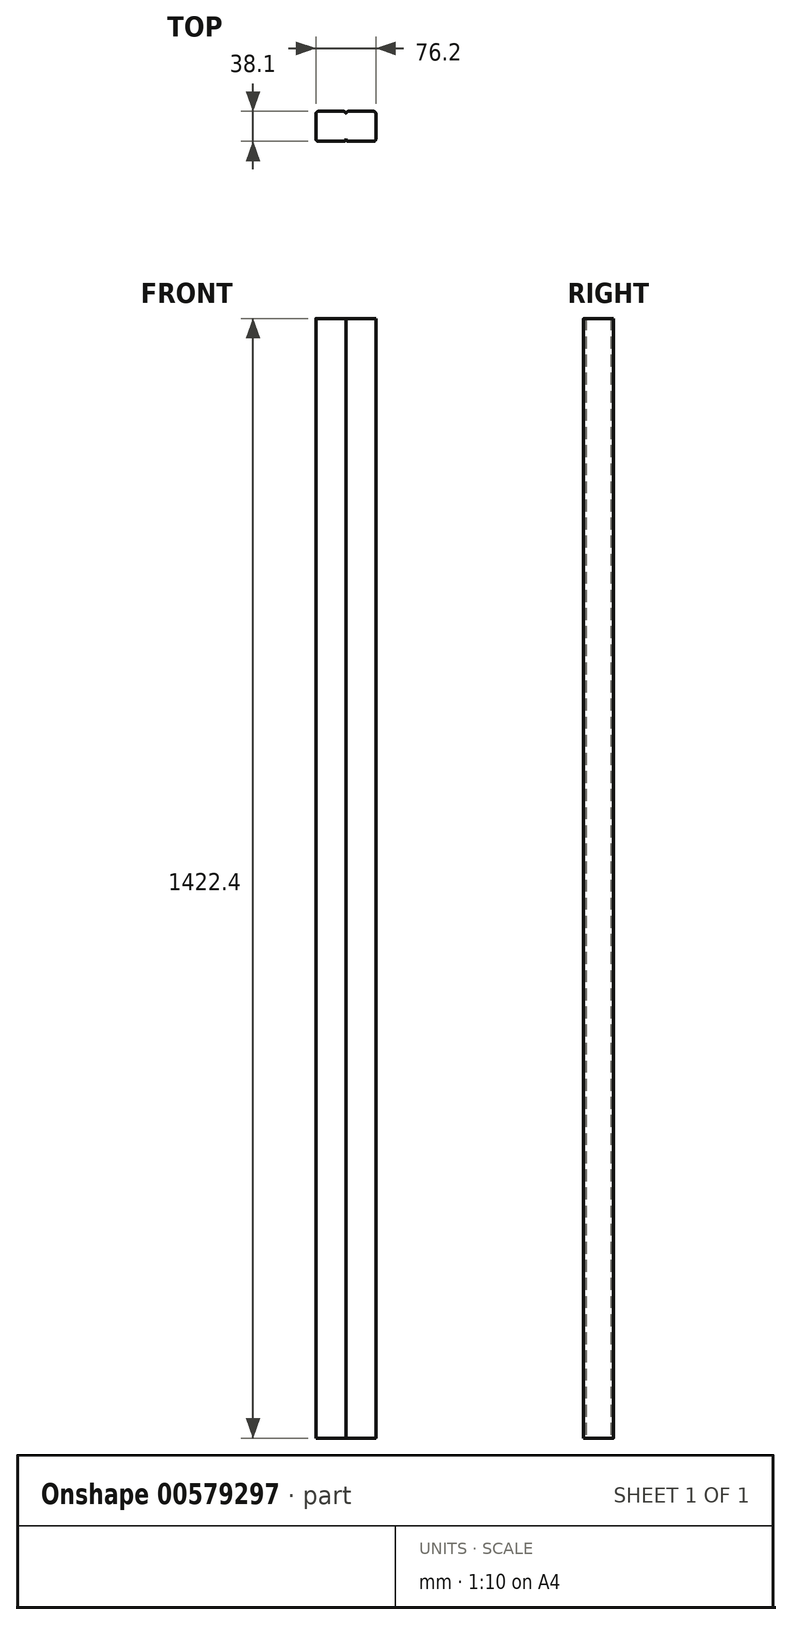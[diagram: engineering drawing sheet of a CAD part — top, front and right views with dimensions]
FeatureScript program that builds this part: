
annotation { "Feature Type Name" : "Feature", "Feature Type Description" : "" }
export const myFeature = defineFeature(function(context is Context, id is Id, definition is map)
    precondition{}
    {
        {
            var Q0;
            Q0=qCreatedBy(makeId("Top.planeOp"),FACE);
            var sketch = newSketch(context, id + "F0", { "sketchPlane" : qUnion([Q0])});
            skLineSegment(sketch, "E0.bottom", {"start": v(34.93, 19.05) * mm, "end": v(3.18, 19.05) * mm});
            skLineSegment(sketch, "E0.top", {"start": v(34.93, -19.05) * mm, "end": v(3.18, -19.05) * mm});
            skLineSegment(sketch, "E0.left", {"start": v(38.1, 15.88) * mm, "end": v(38.1, -15.87) * mm});
            skLineSegment(sketch, "E0.right", {"start": v(-38.1, 15.88) * mm, "end": v(-38.1, -15.88) * mm});
            skPoint(sketch, "E0.middle", {"position": v(0, 0) * mm});
            skLineSegment(sketch, "E1", {"start": v(0, 15.88) * mm, "end": v(0, -15.88) * mm});
            skPoint(sketch, "E2.newPointA", {"position": v(0, 19.05) * mm});
            skPoint(sketch, "E2.newPointB", {"position": v(-38.1, 19.05) * mm});
            skArc(sketch, "E2.filletArc", {"start": v(3.18, 19.05) * mm, "mid": v(0.93, 18.12) * mm, "end": v(0, 15.88) * mm});
            skPoint(sketch, "E3.visualSharp", {"position": v(38.1, 19.05) * mm});
            skArc(sketch, "E3.filletArc", {"start": v(38.1, 15.88) * mm, "mid": v(37.17, 18.12) * mm, "end": v(34.93, 19.05) * mm});
            skPoint(sketch, "E4.visualSharp", {"position": v(38.1, -19.05) * mm});
            skArc(sketch, "E4.filletArc", {"start": v(34.93, -19.05) * mm, "mid": v(37.17, -18.12) * mm, "end": v(38.1, -15.87) * mm});
            skPoint(sketch, "E5.newPointA", {"position": v(-38.1, -19.05) * mm});
            skPoint(sketch, "E5.newPointB", {"position": v(0, -19.05) * mm});
            skArc(sketch, "E5.filletArc", {"start": v(0, -15.88) * mm, "mid": v(0.93, -18.12) * mm, "end": v(3.17, -19.05) * mm});
            skLineSegment(sketch, "E6.bottom", {"start": v(-34.93, 19.05) * mm, "end": v(-3.18, 19.05) * mm});
            skLineSegment(sketch, "E6.top", {"start": v(-34.93, -19.05) * mm, "end": v(-3.18, -19.05) * mm});
            skArc(sketch, "E7.filletArc", {"start": v(-34.93, 19.05) * mm, "mid": v(-37.17, 18.12) * mm, "end": v(-38.1, 15.88) * mm});
            skArc(sketch, "E8.filletArc", {"start": v(0, 15.88) * mm, "mid": v(-0.93, 18.12) * mm, "end": v(-3.18, 19.05) * mm});
            skArc(sketch, "E9.filletArc", {"start": v(-3.18, -19.05) * mm, "mid": v(-0.93, -18.12) * mm, "end": v(0, -15.88) * mm});
            skArc(sketch, "E10.filletArc", {"start": v(-38.1, -15.88) * mm, "mid": v(-37.17, -18.12) * mm, "end": v(-34.93, -19.05) * mm});
            skSolve(sketch);
        }
        {
            var Q0;
            Q0=qSketchRegion(id+"F0",true);
            extrude(context, id + "F1", {"entities" : qUnion([Q0]), "depth" : 1422.4 * mm, "offsetDistance" : 25.4 * mm});
        }
    });
